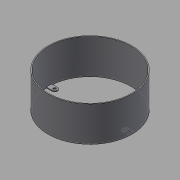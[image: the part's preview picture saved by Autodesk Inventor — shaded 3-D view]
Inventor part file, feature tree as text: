
AUTODESK INVENTOR PART (.ipt)
format: ipt  version: 2015 (Build 190159000, 159)  size: 99,840 bytes
history: native  units: mm
features: extrude x2, sketch x2
ambient origin geometry x8: Origin, YZ Plane, XZ Plane, XY Plane, X Axis, Y Axis, Z Axis, Center Point
bodies: Solid1 (feature_tree)
feature tree (4):
  extrude  "Extrusion1"  Depth=1.0mm
  extrude  "Extrusion2"  [1 undecoded]
  sketch  "Sketch1"  dims[d3=1.0mm d4=0.0mm d5=1.0mm]
  sketch  "Sketch2"  dims[d6=38.0mm d7=0.0mm]
note: 1 required parameter value undecoded (feature->parameter linkage not recoverable at this tier; creation-order binding heuristic only, values carry confidence <= 0.55)
